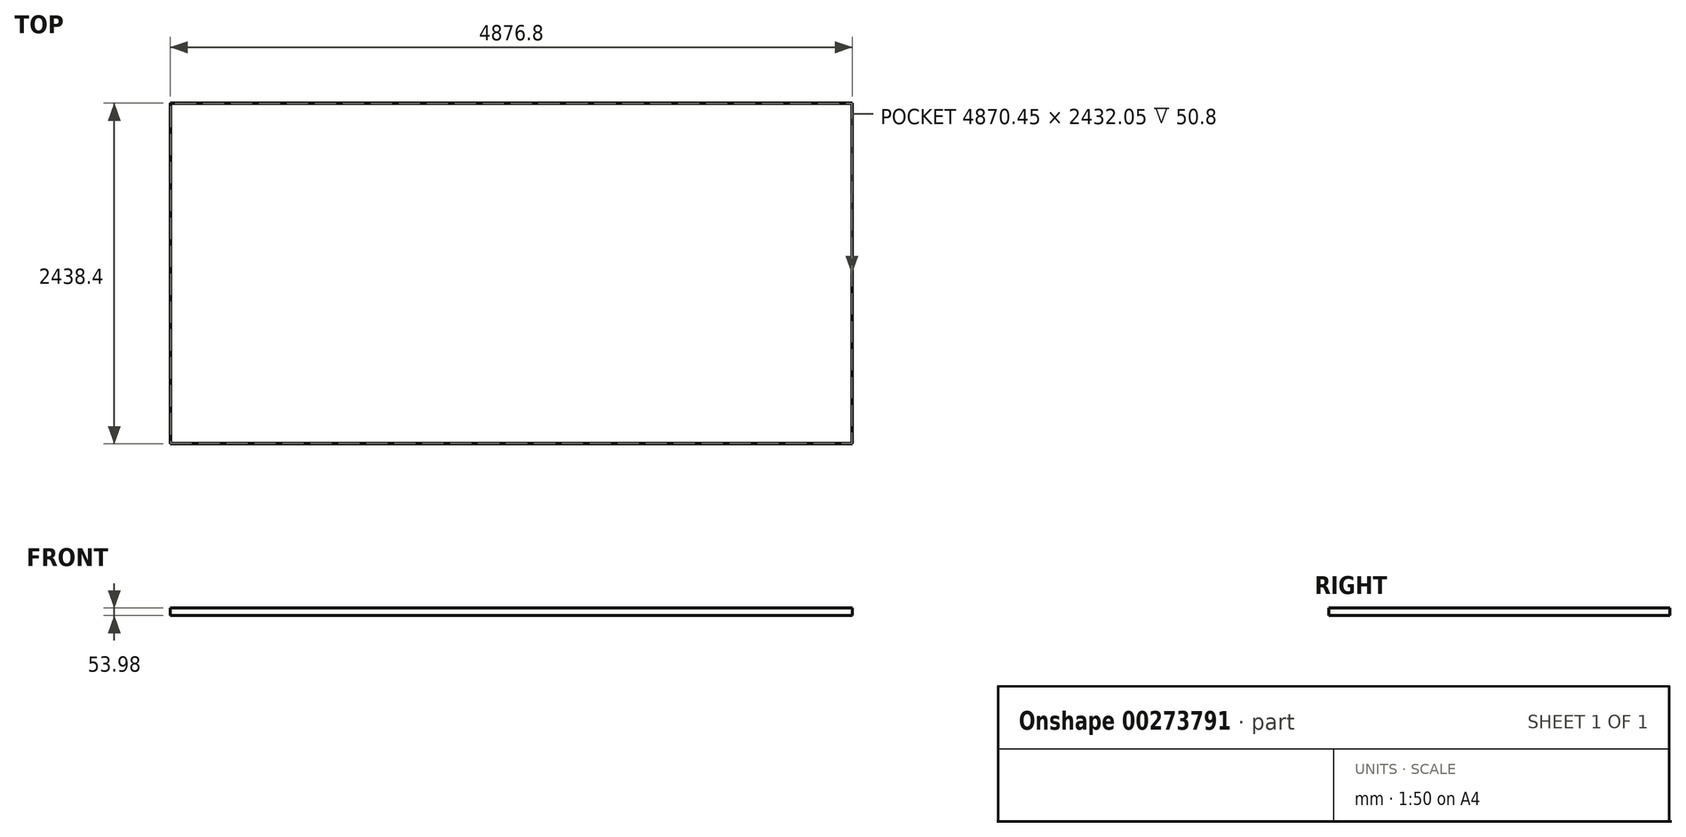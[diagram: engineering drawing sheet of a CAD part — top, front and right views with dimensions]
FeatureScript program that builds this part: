
annotation { "Feature Type Name" : "Feature", "Feature Type Description" : "" }
export const myFeature = defineFeature(function(context is Context, id is Id, definition is map)
    precondition{}
    {
        {
            var Q0;
            Q0=qCreatedBy(makeId("Top.planeOp"),FACE);
            var sketch = newSketch(context, id + "F0", { "sketchPlane" : qUnion([Q0])});
            skLineSegment(sketch, "E0.bottom", {"start": v(0, 0) * mm, "end": v(2438.4, 0) * mm});
            skLineSegment(sketch, "E0.top", {"start": v(0, 2438.4) * mm, "end": v(2438.4, 2438.4) * mm});
            skLineSegment(sketch, "E0.left", {"start": v(0, 0) * mm, "end": v(0, 2438.4) * mm});
            skLineSegment(sketch, "E0.right", {"start": v(2438.4, 0) * mm, "end": v(2438.4, 2438.4) * mm});
            skLineSegment(sketch, "E1.bottom", {"start": v(2438.4, 2438.4) * mm, "end": v(4876.8, 2438.4) * mm});
            skLineSegment(sketch, "E1.top", {"start": v(2438.4, 0) * mm, "end": v(4876.8, 0) * mm});
            skLineSegment(sketch, "E1.left", {"start": v(2438.4, 2438.4) * mm, "end": v(2438.4, 0) * mm});
            skLineSegment(sketch, "E1.right", {"start": v(4876.8, 2438.4) * mm, "end": v(4876.8, 0) * mm});
            skSolve(sketch);
        }
        {
            var Q0;
            Q0 = qSketchRegion(id + "F0", true);
            extrude(context, id + "F1", {"entities" : qUnion([Q0]), "depth" : 3.17 * mm});
        }
        {
            var Q0;
            Q0=makeQuery(id+"F1.opExtrude","CAP_FACE",FACE,{"disambiguationData":[OSD([sQuery(id+"F0.wireOp",EDGE,"E0.bottom"),sQuery(id+"F0.wireOp",EDGE,"E0.top"),sQuery(id+"F0.wireOp",EDGE,"E0.left"),sQuery(id+"F0.wireOp",EDGE,"E1.bottom"),sQuery(id+"F0.wireOp",EDGE,"E1.top"),sQuery(id+"F0.wireOp",EDGE,"E1.right")])],"isStart":false});
            var sketch = newSketch(context, id + "F2", { "sketchPlane" : qUnion([Q0])});
            skLineSegment(sketch, "E2.0", {"start": v(0, 2438.4) * mm, "end": v(4876.8, 2438.4) * mm});
            skLineSegment(sketch, "E3.0", {"start": v(0, 0) * mm, "end": v(0, 2438.4) * mm});
            skLineSegment(sketch, "E4.0", {"start": v(0, 0) * mm, "end": v(4876.8, 0) * mm});
            skLineSegment(sketch, "E5.0", {"start": v(4876.8, 2438.4) * mm, "end": v(4876.8, 0) * mm});
            skLineSegment(sketch, "E6.0", {"start": v(3.18, 2435.22) * mm, "end": v(4873.62, 2435.22) * mm});
            skLineSegment(sketch, "E6.1", {"start": v(3.18, 3.18) * mm, "end": v(3.18, 2435.22) * mm});
            skLineSegment(sketch, "E6.2", {"start": v(3.18, 3.18) * mm, "end": v(4873.62, 3.18) * mm});
            skLineSegment(sketch, "E6.3", {"start": v(4873.62, 2435.22) * mm, "end": v(4873.62, 3.18) * mm});
            skSolve(sketch);
        }
        {
            var Q0;
            Q0 = qSketchRegion(id + "F2", true);
            extrude(context, id + "F3", {"entities" : qUnion([Q0]), "operationType" : NewBodyOperationType.ADD, "depth" : 50.8 * mm});
        }
    });
